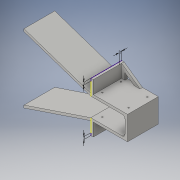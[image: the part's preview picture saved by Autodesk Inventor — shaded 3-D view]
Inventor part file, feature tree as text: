
AUTODESK INVENTOR PART (.ipt)
format: ipt  version: 2016 (Build 200138000, 138)  size: 246,272 bytes
history: native  units: in
note: dims shown in document units (in); Inventor stores cm internally (conversion verified against a paired STEP export)
features: sketch x11, extrude x7, plane x4, hole x1, fillet x1, rib x1
ambient origin geometry x8: Origin, YZ Plane, XZ Plane, XY Plane, X Axis, Y Axis, Z Axis, Center Point
bodies: Solid1 (feature_tree)
feature tree (25):
  extrude  "Extrusion1"  Depth=1.4488in
  extrude  "Extrusion2"  Depth=0.1181in
  sketch  "Sketch3"  dims[d6=0.1181in d7=0.8819in d8=0.0in]
  plane  "Work Plane1"
  extrude  "Extrusion3"  Depth=0.8819in TaperAngle=0.0deg
  hole  "Hole1"  [1 undecoded]
  extrude  "Extrusion4"  Depth=0.128in
  sketch  "Sketch8"  dims[d16=0.128in d17=0.128in d19=0.128in]
  plane  "Work Plane2"
  extrude  "Extrusion5"  Depth=0.128in
  extrude  "Extrusion6"  Depth=0.128in
  fillet  "Fillet1"  Radius=0.128in
  plane  "Work Plane3"
  rib  "Rib1"
  sketch  "Sketch11"  dims[d29=0.1181in d30=0.0in]
  plane  "Work Plane4"
  extrude  "Extrusion7"  Depth=0.128in
  sketch  "Sketch1"  dims[d0=1.6102in d1=1.4488in]
  sketch  "Sketch2"  dims[d2=0.1181in d3=0.0in d5=0.1181in]
  sketch  "Sketch5"  dims[d9=0.1181in d10=0.0in d11=1.4921in]
  sketch  "Sketch6"  dims[d12=1.1339in d13=0.128in]
  sketch  "Sketch7"  dims[d14=0.128in d15=0.128in]
  sketch  "Sketch9"  dims[d20=0.128in d21=0.128in]
  sketch  "Sketch10"  dims[d22=0.0591in d23=0.2362in d24=0.1575in d25=0.0787in d26=90.0deg d27=0.315in d28=0.8108in]
  sketch  "Sketch12"  dims[d31=0.6102in d32=0.0in d33=0.6102in d34=0.0in d35=0.1181in d36=0.1181in d37=0.126in d38=0.8661in d39=0.8661in d40=0.1575in d41=0.1181in d42=0.0in d43=0.0in d44=0.0394in d45=0.0394in d46=0.1181in d49=0.1181in d50=0.1181in d51=0.0in d52=3.937in d53=1.4488in d54=0.0in]
note: 1 required parameter value undecoded (feature->parameter linkage not recoverable at this tier; creation-order binding heuristic only, values carry confidence <= 0.55)
